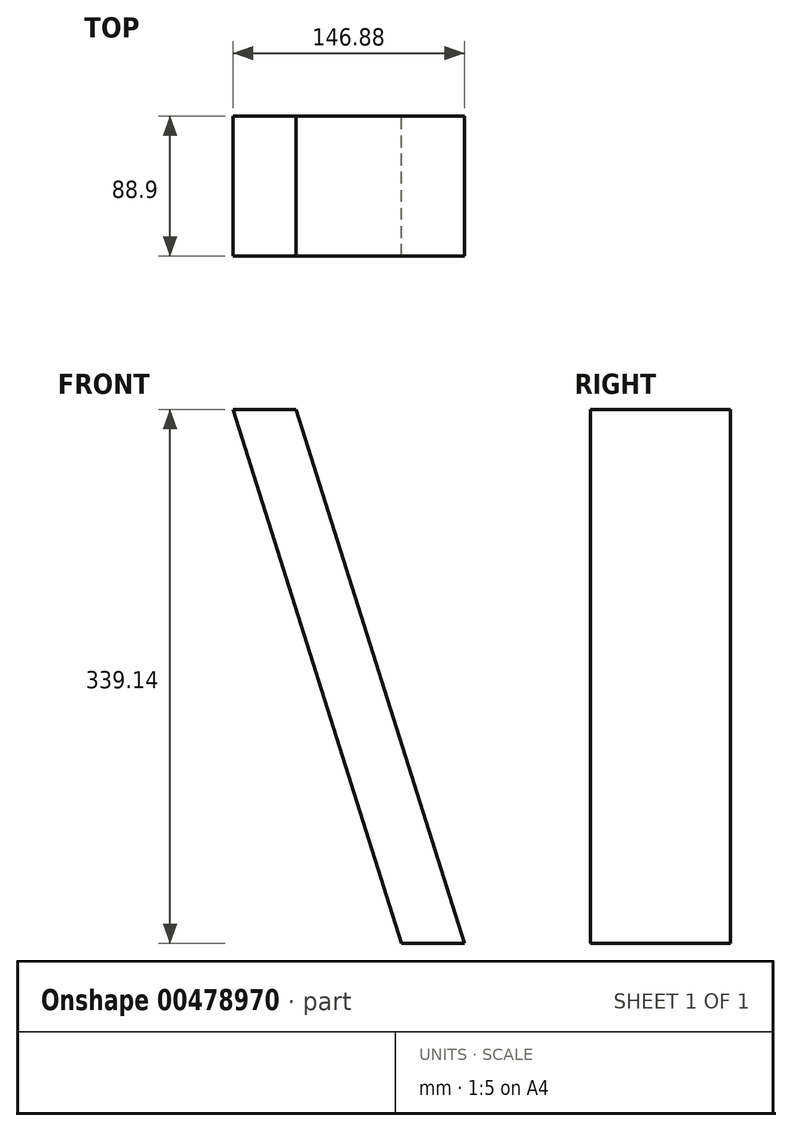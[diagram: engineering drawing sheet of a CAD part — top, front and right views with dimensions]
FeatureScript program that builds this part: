
annotation { "Feature Type Name" : "Feature", "Feature Type Description" : "" }
export const myFeature = defineFeature(function(context is Context, id is Id, definition is map)
    precondition{}
    {
        {
            var Q0;
            Q0=qCreatedBy(makeId("Front.planeOp"),FACE);
            var sketch = newSketch(context, id + "F0", { "sketchPlane" : qUnion([Q0])});
            skLineSegment(sketch, "E0", {"start": v(0, 0) * mm, "end": v(-106.93, 339.14) * mm});
            skLineSegment(sketch, "E1", {"start": v(-106.93, 339.14) * mm, "end": v(-66.98, 339.14) * mm});
            skLineSegment(sketch, "E2", {"start": v(-66.98, 339.14) * mm, "end": v(39.95, 0) * mm});
            skLineSegment(sketch, "E3", {"start": v(39.95, 0) * mm, "end": v(0, 0) * mm});
            skSolve(sketch);
        }
        {
            var Q0;
            Q0 = qSketchRegion(id + "F0", true);
            extrude(context, id + "F1", {"entities" : qUnion([Q0]), "depth" : 88.9 * mm});
        }
    });
